# Revit family: Faucet-Two_Handle-Grohe-Spa-Atrio-21146_Series
name_source: partatom
category: Plumbing Fixtures
units: mm (PartAtom-declared; Revit-internal decimal feet)

## family parameters
Always vertical = No
Cut with Voids When Loaded = No
OmniClass Number = 23.45.55.14
OmniClass Title = Single Faucets
Part Type = Normal
Room Calculation Point = No
Round Connector Dimension = Use Diameter
Shared = Yes
Work Plane-Based = Yes

## types (2) — shared parameters
14215 = No
14216 = No
ASME A112.18.1/CSA B125.1 = Yes
Assembly Code = D2020300
CEC Compliant = Yes
CW Connection = No
CWFU = 1.5
CalGreen Compliant = Yes
Default Elevation = 0"
Description = Atrio Single-Hole Two-Handle L-Size Bathroom Faucet 1.2 GPM
Flow Rate = 1.2 gpm (4.5 l/min)
GROHE EcoJoy = Yes
GROHE SilkMove = Yes
GROHE StarLight = Yes
HW Connection = No
HWFU = 1.5
Height = 11 7/8"
Installation Type = Deck-Mounted
Length = 6 9/16"
Manufacturer = Grohe
NSF 372 = Yes
NSF 61/Section 9 = Yes
Price = Prices may vary. Please consult Manufacturer Representative for most up-to-date price list.
Tempered Water Connection = Yes
Tempered Water Connection Diameter = 3/8"
URL = http://www.grohe.com
Vent Connection = No
WFU = 2
Waste Connection = No
WaterSense = Yes
Width = 5 7/8"

## per-type parameters (varying)
| type | Finish | Material |
| 21146000 | Metal-Grohe-000-StarLight Chrome | Metal-Grohe-000-StarLight Chrome |
| 21146EN0 | Metal-Grohe-EN0-Brushed Nickel InfinityFinish | Metal-Grohe-EN0-Brushed Nickel InfinityFinish |

note: column(s) folded — value = type name in every type: Model

## geometry (parser evidence)
native form markers: Sweep x2
no freeform markers — native parametric forms only
